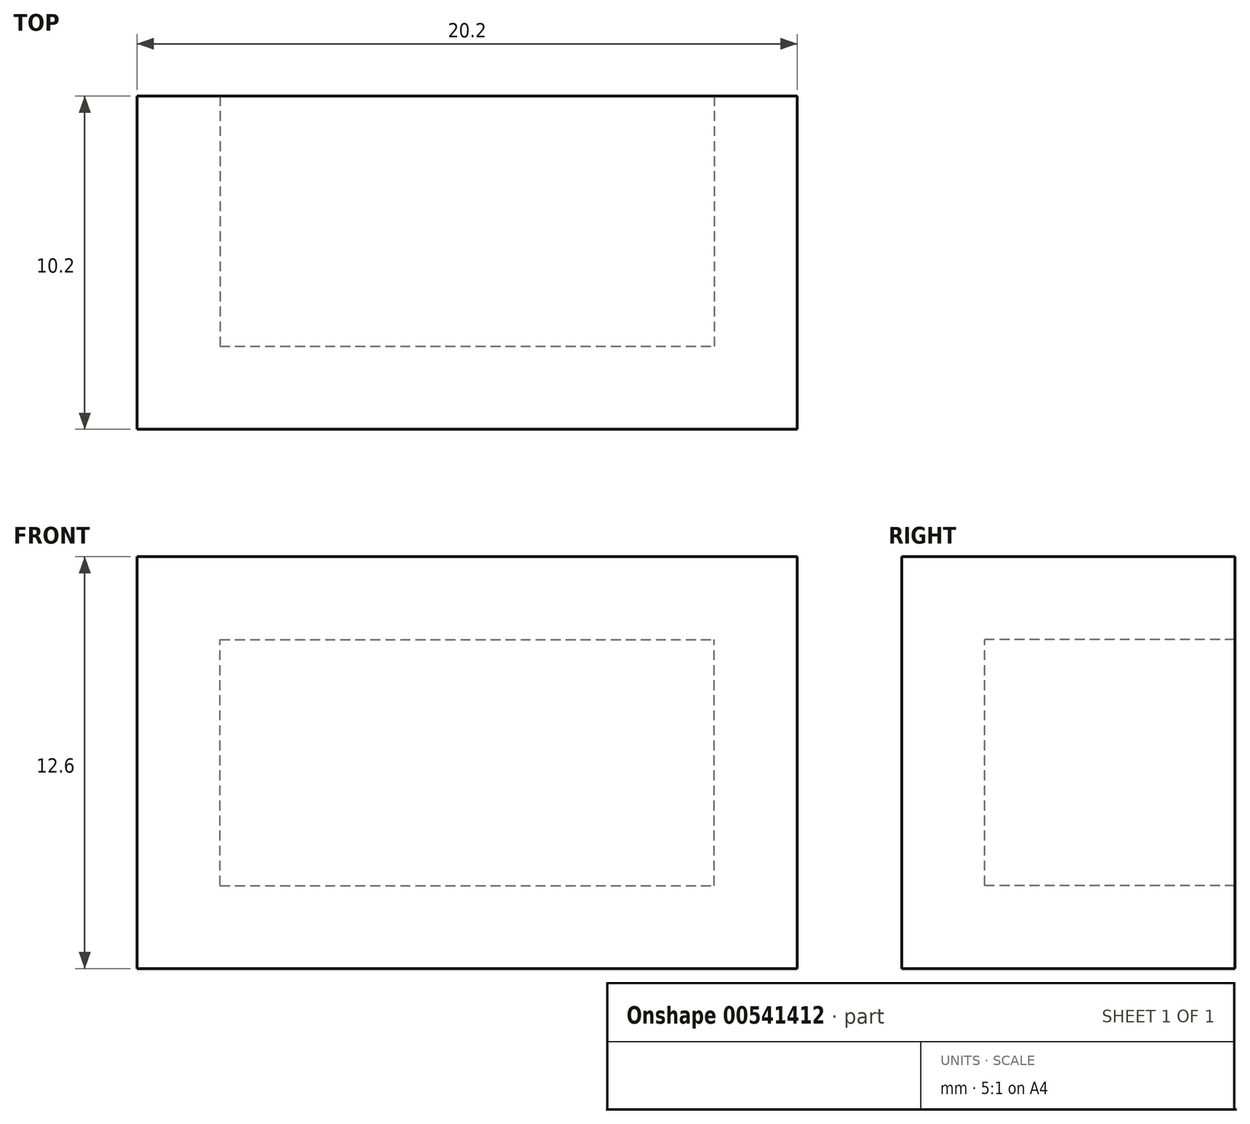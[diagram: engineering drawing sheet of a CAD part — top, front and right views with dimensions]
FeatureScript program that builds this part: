
annotation { "Feature Type Name" : "Feature", "Feature Type Description" : "" }
export const myFeature = defineFeature(function(context is Context, id is Id, definition is map)
    precondition{}
    {
        {
            var Q0;
            Q0=qCreatedBy(makeId("Front.planeOp"),FACE);
            var sketch = newSketch(context, id + "F0", { "sketchPlane" : qUnion([Q0])});
            skLineSegment(sketch, "E0.bottom", {"start": v(-10.1, -6.3) * mm, "end": v(10.1, -6.3) * mm});
            skLineSegment(sketch, "E0.top", {"start": v(-10.1, 6.3) * mm, "end": v(10.1, 6.3) * mm});
            skLineSegment(sketch, "E0.left", {"start": v(-10.1, -6.3) * mm, "end": v(-10.1, 6.3) * mm});
            skLineSegment(sketch, "E0.right", {"start": v(10.1, -6.3) * mm, "end": v(10.1, 6.3) * mm});
            skPoint(sketch, "E0.middle", {"position": v(0, 0) * mm});
            skSolve(sketch);
        }
        {
            var Q0;
            Q0 = qSketchRegion(id + "F0", true);
            extrude(context, id + "F1", {"entities" : qUnion([Q0]), "oppositeDirection" : true, "depth" : 10.2 * mm, "offsetDistance" : 25.4 * mm});
        }
        {
            var Q0;
            Q0=makeQuery(id+"F1.opExtrude","CAP_FACE",FACE,{"disambiguationData":[OSD([sQuery(id+"F0.wireOp",EDGE,"E0.bottom"),sQuery(id+"F0.wireOp",EDGE,"E0.top"),sQuery(id+"F0.wireOp",EDGE,"E0.left"),sQuery(id+"F0.wireOp",EDGE,"E0.right")])],"isStart":false});
            shell(context, id + "F2", {"entities" : qUnion([Q0]), "thickness" : 2.54 * mm});
        }
    });
